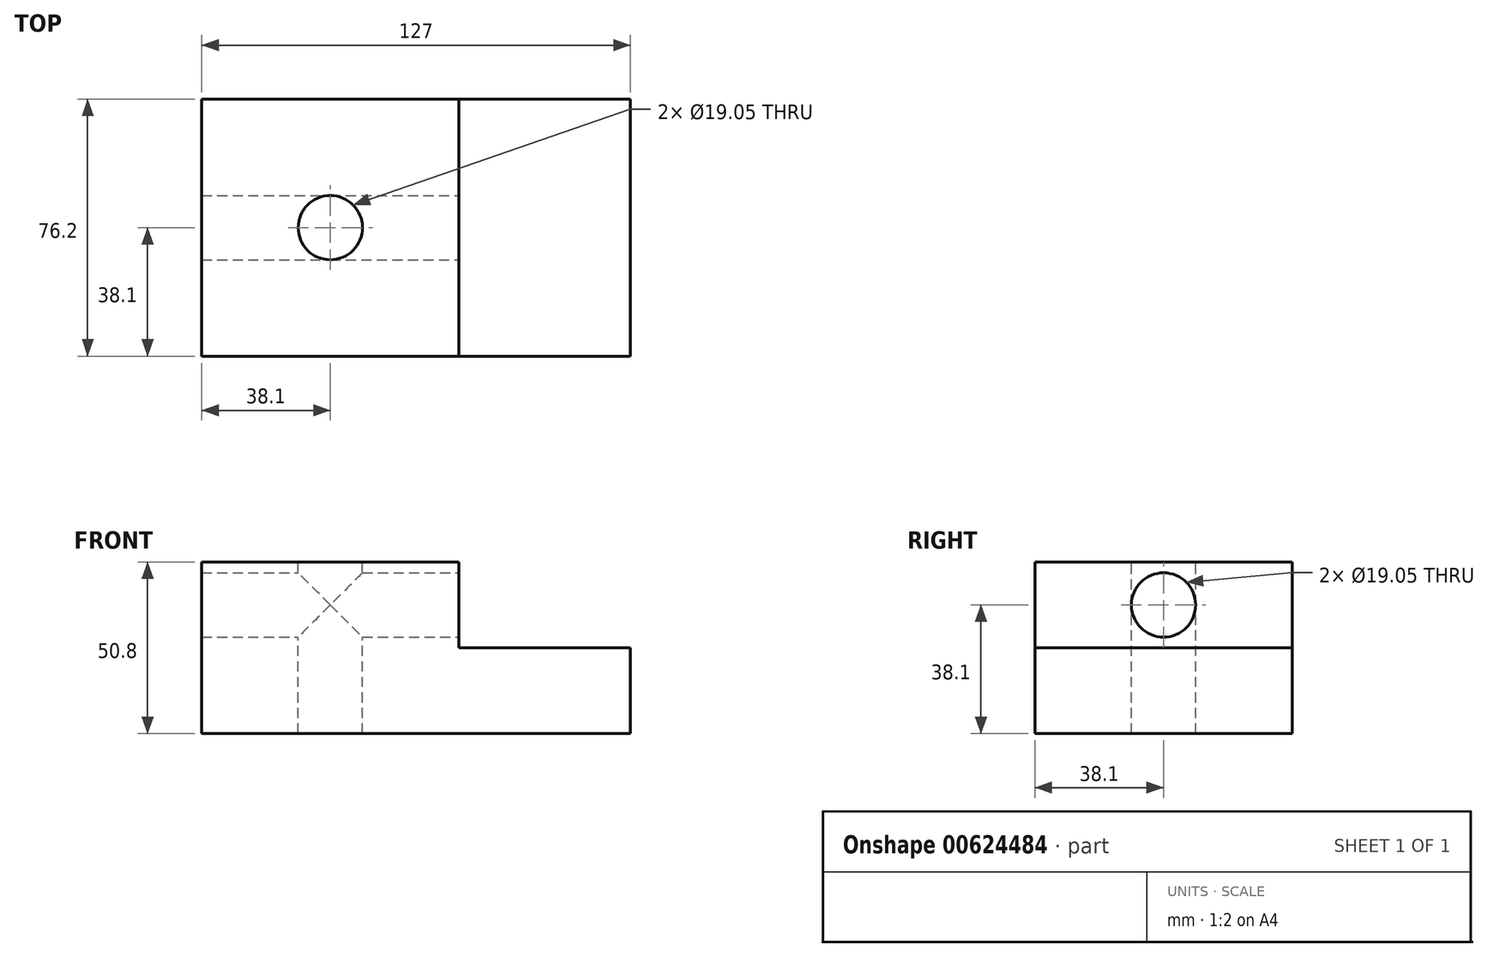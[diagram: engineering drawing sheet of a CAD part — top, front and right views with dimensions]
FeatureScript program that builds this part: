
annotation { "Feature Type Name" : "Feature", "Feature Type Description" : "" }
export const myFeature = defineFeature(function(context is Context, id is Id, definition is map)
    precondition{}
    {
        {
            var Q0;
            Q0=qCreatedBy(makeId("Front.planeOp"),FACE);
            var sketch = newSketch(context, id + "F0", { "sketchPlane" : qUnion([Q0])});
            skLineSegment(sketch, "E0.bottom", {"start": v(12.7, 25.4) * mm, "end": v(-63.5, 25.4) * mm});
            skLineSegment(sketch, "E0.top", {"start": v(63.5, -25.4) * mm, "end": v(-63.5, -25.4) * mm});
            skLineSegment(sketch, "E0.left", {"start": v(63.5, 0) * mm, "end": v(63.5, -25.4) * mm});
            skLineSegment(sketch, "E0.right", {"start": v(-63.5, 25.4) * mm, "end": v(-63.5, -25.4) * mm});
            skPoint(sketch, "E0.middle", {"position": v(0, 0) * mm});
            skPoint(sketch, "E1.middle.positionSnap0", {"position": v(-63.5, 0) * mm});
            skPoint(sketch, "E1.centerSnap0", {"position": v(-63.5, 0) * mm});
            skLineSegment(sketch, "E2", {"start": v(63.5, 0) * mm, "end": v(12.7, 0) * mm});
            skLineSegment(sketch, "E3", {"start": v(12.7, 0) * mm, "end": v(12.7, 25.4) * mm});
            skSolve(sketch);
        }
        {
            var Q0;
            Q0 = qSketchRegion(id + "F0", true);
            extrude(context, id + "F1", {"entities" : qUnion([Q0]), "depth" : 76.2 * mm, "offsetDistance" : 25.4 * mm});
        }
        {
            var Q0;
            Q0=makeQuery(id+"F1.opExtrude","SWEPT_FACE",FACE,{"disambiguationData":[OSD([sQuery(id+"F0.wireOp",EDGE,"E0.bottom")])]});
            var sketch = newSketch(context, id + "F2", { "sketchPlane" : qUnion([Q0])});
            skLineSegment(sketch, "E4", {"start": v(12.7, -76.2) * mm, "end": v(-63.5, 0) * mm});
            skLineSegment(sketch, "E5", {"start": v(-63.5, -76.2) * mm, "end": v(12.7, 0) * mm});
            skCircle(sketch, "E6", {"center": v(-25.4, -38.1) * mm, "radius": 14.3 * mm});
            skSolve(sketch);
        }
        {
            var Q0;
            Q0=sQuery(id+"F2.wireOp",VERTEX,"E6.center");
            var Q1;
            Q1=makeQuery(id+"F1.opExtrude","SWEPT_BODY",BODY,{"disambiguationData":[OSD([sQuery(id+"F0.wireOp",EDGE,"E0.bottom"),sQuery(id+"F0.wireOp",EDGE,"E0.top"),sQuery(id+"F0.wireOp",EDGE,"E0.left"),sQuery(id+"F0.wireOp",EDGE,"E0.right"),sQuery(id+"F0.wireOp",EDGE,"E2"),sQuery(id+"F0.wireOp",EDGE,"E3")])]});
            hole(context, id + "F3", {"style" : HoleStyle.SIMPLE, "endStyle" : HoleEndStyle.THROUGH, "holeDiameter" : 19.05 * mm, "majorDiameter" : 6.35 * mm, "isTappedThrough" : true, "tappedDepth" : 12.7 * mm, "tapClearance" : 3, "locations" : qUnion([Q0]), "scope" : qUnion([Q1])});
        }
        {
            var Q0;
            Q0=makeQuery(id+"F1.opExtrude","SWEPT_FACE",FACE,{"disambiguationData":[OSD([sQuery(id+"F0.wireOp",EDGE,"E3")])]});
            var sketch = newSketch(context, id + "F4", { "sketchPlane" : qUnion([Q0])});
            skLineSegment(sketch, "E7", {"start": v(-76.2, 0) * mm, "end": v(0, 25.4) * mm});
            skLineSegment(sketch, "E8", {"start": v(0, 0) * mm, "end": v(-76.2, 25.4) * mm});
            skCircle(sketch, "E9", {"center": v(-38.1, 12.7) * mm, "radius": 6 * mm});
            skSolve(sketch);
        }
        {
            var Q0;
            Q0=sQuery(id+"F4.wireOp",VERTEX,"E9.center");
            var Q1;
            Q1=makeQuery(id+"F1.opExtrude","SWEPT_BODY",BODY,{"disambiguationData":[OSD([sQuery(id+"F0.wireOp",EDGE,"E0.bottom"),sQuery(id+"F0.wireOp",EDGE,"E0.top"),sQuery(id+"F0.wireOp",EDGE,"E0.left"),sQuery(id+"F0.wireOp",EDGE,"E0.right"),sQuery(id+"F0.wireOp",EDGE,"E2"),sQuery(id+"F0.wireOp",EDGE,"E3")])]});
            hole(context, id + "F5", {"style" : HoleStyle.SIMPLE, "endStyle" : HoleEndStyle.THROUGH, "holeDiameter" : 19.05 * mm, "majorDiameter" : 6.35 * mm, "isTappedThrough" : true, "tappedDepth" : 12.7 * mm, "tapClearance" : 3, "locations" : qUnion([Q0]), "scope" : qUnion([Q1])});
        }
    });
